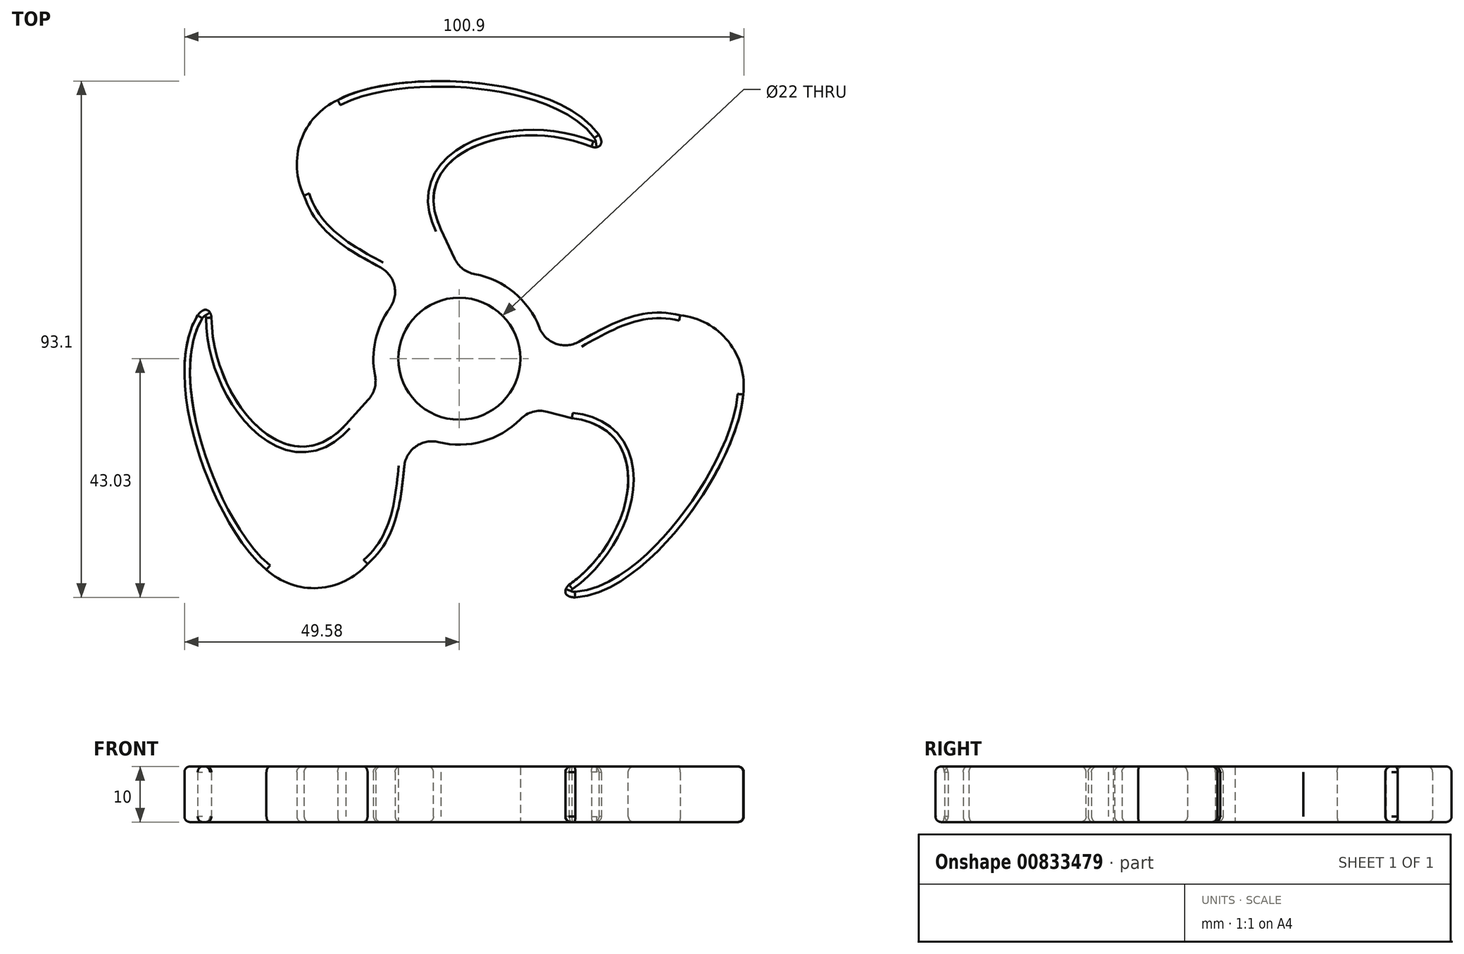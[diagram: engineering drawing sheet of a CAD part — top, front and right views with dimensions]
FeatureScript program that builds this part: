
annotation { "Feature Type Name" : "Feature", "Feature Type Description" : "" }
export const myFeature = defineFeature(function(context is Context, id is Id, definition is map)
    precondition{}
    {
        {
            var Q0;
            Q0=qCreatedBy(makeId("Top.planeOp"),FACE);
            var sketch = newSketch(context, id + "F0", { "sketchPlane" : qUnion([Q0])});
            skArc(sketch, "E0", {"start": v(-34.79, -38.03) * mm, "mid": v(-25.45, -41.34) * mm, "end": v(-16.55, -36.98) * mm});
            skFitSpline(sketch, "E1", {"points": [v(-34.79, -38.03) * mm, v(-47.19, 7.84) * mm], "startDerivative": vector(-28.32, 23.04) * mm, "endDerivative": vector(21.26, 34.04) * mm});
            skFitSpline(sketch, "E2", {"points": [v(-44.7, 7.43) * mm, v(-20.48, -11.86) * mm], "startDerivative": vector(0.28, -44.9) * mm, "endDerivative": vector(31.1, 34.9) * mm});
            skFitSpline(sketch, "E3", {"points": [v(-16.55, -36.98) * mm, v(-8.17, -8.78) * mm], "startDerivative": vector(24.18, 20.97) * mm, "endDerivative": vector(9.05, 30.3) * mm});
            skLineSegment(sketch, "E4", {"start": v(-20.48, -11.86) * mm, "end": v(-16.4, -7.38) * mm});
            skFitSpline(sketch, "E5", {"points": [v(-44.7, 7.43) * mm, v(-47.19, 7.84) * mm], "startDerivative": vector(-0.43, 4.2) * mm, "endDerivative": vector(-3.7, -5.07) * mm});
            skArc(sketch, "E6", {"start": v(51.22, -6.44) * mm, "mid": v(48.53, 3.1) * mm, "end": v(39.84, 7.85) * mm});
            skFitSpline(sketch, "E7", {"points": [v(51.22, -6.44) * mm, v(20.9, -43.03) * mm], "startDerivative": vector(-2.48, -36.42) * mm, "endDerivative": vector(-40.07, -2.27) * mm});
            skFitSpline(sketch, "E8", {"points": [v(19.8, -40.76) * mm, v(20.29, -10.72) * mm], "startDerivative": vector(36.5, 26.13) * mm, "endDerivative": vector(-46.45, 5.27) * mm});
            skFitSpline(sketch, "E9", {"points": [v(39.84, 7.85) * mm, v(11.97, -1.57) * mm], "startDerivative": vector(-31.08, 7.66) * mm, "endDerivative": vector(-29.97, -10.08) * mm});
            skLineSegment(sketch, "E10", {"start": v(20.29, -10.72) * mm, "end": v(15.85, -9.56) * mm});
            skFitSpline(sketch, "E11", {"points": [v(19.8, -40.76) * mm, v(20.9, -43.03) * mm], "startDerivative": vector(-3.18, -2.78) * mm, "endDerivative": vector(6.27, -0.1) * mm});
            skArc(sketch, "E12", {"start": v(-21.93, 46.65) * mm, "mid": v(-28.58, 39.31) * mm, "end": v(-28, 29.42) * mm});
            skFitSpline(sketch, "E13", {"points": [v(-21.93, 46.65) * mm, v(25.17, 40.37) * mm], "startDerivative": vector(32.19, 17.22) * mm, "endDerivative": vector(23.19, -32.76) * mm});
            skFitSpline(sketch, "E14", {"points": [v(23.84, 38.23) * mm, v(-3.31, 23.35) * mm], "startDerivative": vector(-41.52, 17.08) * mm, "endDerivative": vector(20.18, -42.17) * mm});
            skFitSpline(sketch, "E15", {"points": [v(-28, 29.42) * mm, v(-5.23, 10.8) * mm], "startDerivative": vector(10, -30.4) * mm, "endDerivative": vector(24.45, -20.05) * mm});
            skLineSegment(sketch, "E16", {"start": v(-3.31, 23.35) * mm, "end": v(-0.85, 18.05) * mm});
            skFitSpline(sketch, "E17", {"points": [v(23.84, 38.23) * mm, v(25.17, 40.37) * mm], "startDerivative": vector(4.05, -1.22) * mm, "endDerivative": vector(-3.25, 5.36) * mm});
            skLineSegment(sketch, "E18", {"start": v(11.97, -1.57) * mm, "end": v(11.88, -1.62) * mm});
            skLineSegment(sketch, "E19", {"start": v(-8.17, -8.78) * mm, "end": v(-8.17, -8.78) * mm});
            skArc(sketch, "E20.trimOffspring", {"start": v(-8.17, -8.78) * mm, "mid": v(-8.17, -8.78) * mm, "end": v(-8.17, -8.78) * mm});
            skArc(sketch, "E21", {"start": v(-12.54, 9.11) * mm, "mid": v(-15.14, 3.32) * mm, "end": v(-15.2, -3.04) * mm});
            skArc(sketch, "E22.trimOffspring", {"start": v(14.45, 5.6) * mm, "mid": v(9.87, 11.95) * mm, "end": v(2.79, 15.25) * mm});
            skArc(sketch, "E23.trimOffspring", {"start": v(-3.75, -15.04) * mm, "mid": v(4.2, -14.92) * mm, "end": v(11.03, -10.89) * mm});
            skCircle(sketch, "E24", {"center": v(0, 0) * mm, "radius": 11 * mm});
            skPoint(sketch, "E25.visualSharp", {"position": v(-9.06, -12.58) * mm});
            skArc(sketch, "E25.filletArc", {"start": v(-3.75, -15.04) * mm, "mid": v(-7.83, -15.8) * mm, "end": v(-9.93, -19.39) * mm});
            skPoint(sketch, "E26.visualSharp", {"position": v(12.78, -8.76) * mm});
            skArc(sketch, "E26.filletArc", {"start": v(15.85, -9.56) * mm, "mid": v(13.26, -9.58) * mm, "end": v(11.03, -10.89) * mm});
            skPoint(sketch, "E27.visualSharp", {"position": v(15.5, -0.15) * mm});
            skArc(sketch, "E27.filletArc", {"start": v(14.45, 5.6) * mm, "mid": v(17.43, 2.7) * mm, "end": v(21.57, 3.06) * mm});
            skPoint(sketch, "E28.visualSharp", {"position": v(0.34, 15.5) * mm});
            skArc(sketch, "E28.filletArc", {"start": v(-0.85, 18.05) * mm, "mid": v(0.63, 16.2) * mm, "end": v(2.79, 15.25) * mm});
            skPoint(sketch, "E29.visualSharp", {"position": v(-8.35, 13.06) * mm});
            skArc(sketch, "E29.filletArc", {"start": v(-12.54, 9.11) * mm, "mid": v(-11.7, 13.15) * mm, "end": v(-14.2, 16.44) * mm});
            skPoint(sketch, "E30.visualSharp", {"position": v(-14.55, -5.34) * mm});
            skArc(sketch, "E30.filletArc", {"start": v(-16.4, -7.38) * mm, "mid": v(-15.28, -5.35) * mm, "end": v(-15.2, -3.04) * mm});
            skSolve(sketch);
        }
        {
            var Q0;
            Q0 = qSketchRegion(id + "F0", true);
            extrude(context, id + "F1", {"entities" : qUnion([Q0]), "depth" : 10 * mm, "offsetDistance" : 25 * mm});
        }
        {
            var Q0;
            Q0=makeQuery(id+"F1.opExtrude","CAP_EDGE",EDGE,{"disambiguationData":[OSD([sQuery(id+"F0.wireOp",EDGE,"E3")])],"isStart":false});
            var Q1;
            Q1=makeQuery(id+"F1.opExtrude","CAP_EDGE",EDGE,{"disambiguationData":[OSD([sQuery(id+"F0.wireOp",EDGE,"E23.trimOffspring")])],"isStart":false});
            var Q2;
            Q2=makeQuery(id+"F1.opExtrude","CAP_EDGE",EDGE,{"disambiguationData":[OSD([sQuery(id+"F0.wireOp",EDGE,"E0")])],"isStart":false});
            var Q3;
            Q3=makeQuery(id+"F1.opExtrude","CAP_EDGE",EDGE,{"disambiguationData":[OSD([sQuery(id+"F0.wireOp",EDGE,"E10")])],"isStart":false});
            var Q4;
            Q4=makeQuery(id+"F1.opExtrude","CAP_EDGE",EDGE,{"disambiguationData":[OSD([sQuery(id+"F0.wireOp",EDGE,"E8")])],"isStart":false});
            var Q5;
            Q5=makeQuery(id+"F1.opExtrude","CAP_EDGE",EDGE,{"disambiguationData":[OSD([sQuery(id+"F0.wireOp",EDGE,"E11")])],"isStart":false});
            var Q6;
            Q6=makeQuery(id+"F1.opExtrude","CAP_EDGE",EDGE,{"disambiguationData":[OSD([sQuery(id+"F0.wireOp",EDGE,"E7")])],"isStart":false});
            var Q7;
            Q7=makeQuery(id+"F1.opExtrude","CAP_EDGE",EDGE,{"disambiguationData":[OSD([sQuery(id+"F0.wireOp",EDGE,"E6")])],"isStart":false});
            var Q8;
            Q8=makeQuery(id+"F1.opExtrude","CAP_EDGE",EDGE,{"disambiguationData":[OSD([sQuery(id+"F0.wireOp",EDGE,"E9")])],"isStart":false});
            var Q9;
            Q9=makeQuery(id+"F1.opExtrude","CAP_EDGE",EDGE,{"disambiguationData":[OSD([sQuery(id+"F0.wireOp",EDGE,"E22.trimOffspring")])],"isStart":false});
            var Q10;
            Q10=makeQuery(id+"F1.opExtrude","CAP_EDGE",EDGE,{"disambiguationData":[OSD([sQuery(id+"F0.wireOp",EDGE,"E16")])],"isStart":false});
            var Q11;
            Q11=makeQuery(id+"F1.opExtrude","CAP_EDGE",EDGE,{"disambiguationData":[OSD([sQuery(id+"F0.wireOp",EDGE,"E14")])],"isStart":false});
            var Q12;
            Q12=makeQuery(id+"F1.opExtrude","CAP_EDGE",EDGE,{"disambiguationData":[OSD([sQuery(id+"F0.wireOp",EDGE,"E17")])],"isStart":false});
            var Q13;
            Q13=makeQuery(id+"F1.opExtrude","CAP_EDGE",EDGE,{"disambiguationData":[OSD([sQuery(id+"F0.wireOp",EDGE,"E13")])],"isStart":false});
            var Q14;
            Q14=makeQuery(id+"F1.opExtrude","CAP_EDGE",EDGE,{"disambiguationData":[OSD([sQuery(id+"F0.wireOp",EDGE,"E12")])],"isStart":false});
            var Q15;
            Q15=makeQuery(id+"F1.opExtrude","CAP_EDGE",EDGE,{"disambiguationData":[OSD([sQuery(id+"F0.wireOp",EDGE,"E15")])],"isStart":false});
            var Q16;
            Q16=makeQuery(id+"F1.opExtrude","CAP_EDGE",EDGE,{"disambiguationData":[OSD([sQuery(id+"F0.wireOp",EDGE,"E21")])],"isStart":false});
            var Q17;
            Q17=makeQuery(id+"F1.opExtrude","CAP_EDGE",EDGE,{"disambiguationData":[OSD([sQuery(id+"F0.wireOp",EDGE,"E4")])],"isStart":false});
            var Q18;
            Q18=makeQuery(id+"F1.opExtrude","CAP_EDGE",EDGE,{"disambiguationData":[OSD([sQuery(id+"F0.wireOp",EDGE,"E2")])],"isStart":false});
            fillet(context, id + "F2", {"entities" : qUnion([Q0, Q1, Q2, Q3, Q4, Q5, Q6, Q7, Q8, Q9, Q10, Q11, Q12, Q13, Q14, Q15, Q16, Q17, Q18]), "radius" : 1 * mm, "tangentPropagation" : true, "allowEdgeOverflow" : false});
        }
        {
            var Q0;
            Q0=makeQuery(id+"F1.opExtrude","CAP_EDGE",EDGE,{"disambiguationData":[OSD([sQuery(id+"F0.wireOp",EDGE,"E0")])],"isStart":true});
            var Q1;
            Q1=makeQuery(id+"F1.opExtrude","CAP_EDGE",EDGE,{"disambiguationData":[OSD([sQuery(id+"F0.wireOp",EDGE,"E3")])],"isStart":true});
            var Q2;
            Q2=makeQuery(id+"F1.opExtrude","CAP_EDGE",EDGE,{"disambiguationData":[OSD([sQuery(id+"F0.wireOp",EDGE,"E2")])],"isStart":true});
            var Q3;
            Q3=makeQuery(id+"F1.opExtrude","CAP_EDGE",EDGE,{"disambiguationData":[OSD([sQuery(id+"F0.wireOp",EDGE,"E4")])],"isStart":true});
            var Q4;
            Q4=makeQuery(id+"F1.opExtrude","CAP_EDGE",EDGE,{"disambiguationData":[OSD([sQuery(id+"F0.wireOp",EDGE,"E21")])],"isStart":true});
            var Q5;
            Q5=makeQuery(id+"F1.opExtrude","CAP_EDGE",EDGE,{"disambiguationData":[OSD([sQuery(id+"F0.wireOp",EDGE,"E15")])],"isStart":true});
            var Q6;
            Q6=makeQuery(id+"F1.opExtrude","CAP_EDGE",EDGE,{"disambiguationData":[OSD([sQuery(id+"F0.wireOp",EDGE,"E12")])],"isStart":true});
            var Q7;
            Q7=makeQuery(id+"F1.opExtrude","CAP_EDGE",EDGE,{"disambiguationData":[OSD([sQuery(id+"F0.wireOp",EDGE,"E13")])],"isStart":true});
            var Q8;
            Q8=makeQuery(id+"F1.opExtrude","CAP_EDGE",EDGE,{"disambiguationData":[OSD([sQuery(id+"F0.wireOp",EDGE,"E17")])],"isStart":true});
            var Q9;
            Q9=makeQuery(id+"F1.opExtrude","CAP_EDGE",EDGE,{"disambiguationData":[OSD([sQuery(id+"F0.wireOp",EDGE,"E14")])],"isStart":true});
            var Q10;
            Q10=makeQuery(id+"F1.opExtrude","CAP_EDGE",EDGE,{"disambiguationData":[OSD([sQuery(id+"F0.wireOp",EDGE,"E16")])],"isStart":true});
            var Q11;
            Q11=makeQuery(id+"F1.opExtrude","CAP_EDGE",EDGE,{"disambiguationData":[OSD([sQuery(id+"F0.wireOp",EDGE,"E22.trimOffspring")])],"isStart":true});
            var Q12;
            Q12=makeQuery(id+"F1.opExtrude","CAP_EDGE",EDGE,{"disambiguationData":[OSD([sQuery(id+"F0.wireOp",EDGE,"E9")])],"isStart":true});
            var Q13;
            Q13=makeQuery(id+"F1.opExtrude","CAP_EDGE",EDGE,{"disambiguationData":[OSD([sQuery(id+"F0.wireOp",EDGE,"E6")])],"isStart":true});
            var Q14;
            Q14=makeQuery(id+"F1.opExtrude","CAP_EDGE",EDGE,{"disambiguationData":[OSD([sQuery(id+"F0.wireOp",EDGE,"E7")])],"isStart":true});
            var Q15;
            Q15=makeQuery(id+"F1.opExtrude","CAP_EDGE",EDGE,{"disambiguationData":[OSD([sQuery(id+"F0.wireOp",EDGE,"E11")])],"isStart":true});
            var Q16;
            Q16=makeQuery(id+"F1.opExtrude","CAP_EDGE",EDGE,{"disambiguationData":[OSD([sQuery(id+"F0.wireOp",EDGE,"E8")])],"isStart":true});
            var Q17;
            Q17=makeQuery(id+"F1.opExtrude","CAP_EDGE",EDGE,{"disambiguationData":[OSD([sQuery(id+"F0.wireOp",EDGE,"E10")])],"isStart":true});
            var Q18;
            Q18=makeQuery(id+"F1.opExtrude","CAP_EDGE",EDGE,{"disambiguationData":[OSD([sQuery(id+"F0.wireOp",EDGE,"E23.trimOffspring")])],"isStart":true});
            fillet(context, id + "F3", {"entities" : qUnion([Q0, Q1, Q2, Q3, Q4, Q5, Q6, Q7, Q8, Q9, Q10, Q11, Q12, Q13, Q14, Q15, Q16, Q17, Q18]), "radius" : 1 * mm, "tangentPropagation" : true, "allowEdgeOverflow" : false});
        }
    });
